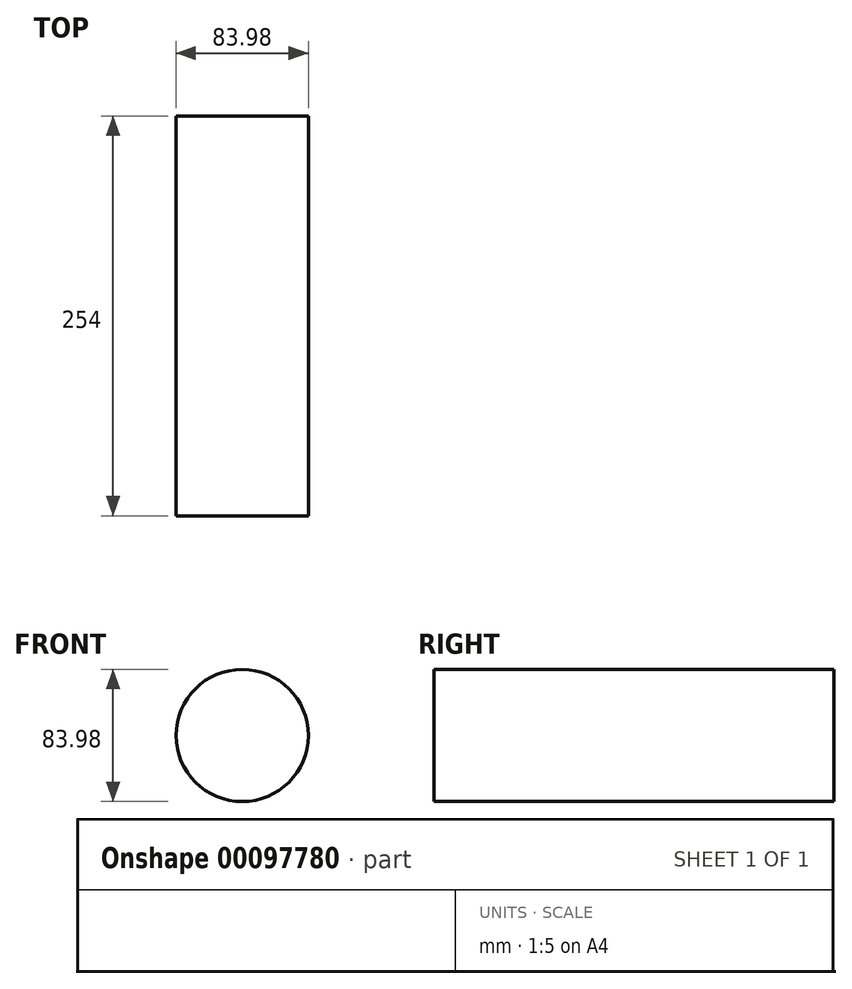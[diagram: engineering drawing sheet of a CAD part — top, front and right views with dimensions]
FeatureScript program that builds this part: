
annotation { "Feature Type Name" : "Feature", "Feature Type Description" : "" }
export const myFeature = defineFeature(function(context is Context, id is Id, definition is map)
    precondition{}
    {
        {
            var Q0;
            Q0=qCreatedBy(makeId("Front.planeOp"),FACE);
            var sketch = newSketch(context, id + "F0", { "sketchPlane" : qUnion([Q0])});
            skCircle(sketch, "E0", {"center": v(0, 0) * mm, "radius": 41.99 * mm});
            skSolve(sketch);
        }
        {
            var Q0;
            Q0=makeQuery(id+"F0.imprint","IMPRINT",FACE,{"disambiguationData":[TD([[makeQuery(id+"F0.imprint","IMPRINT",EDGE,{"derivedFrom":sQuery(id+"F0.wireOp",EDGE,"E0")}),1.0]])]});
            extrude(context, id + "F1", {"entities" : qUnion([Q0]), "depth" : 254 * mm});
        }
    });
